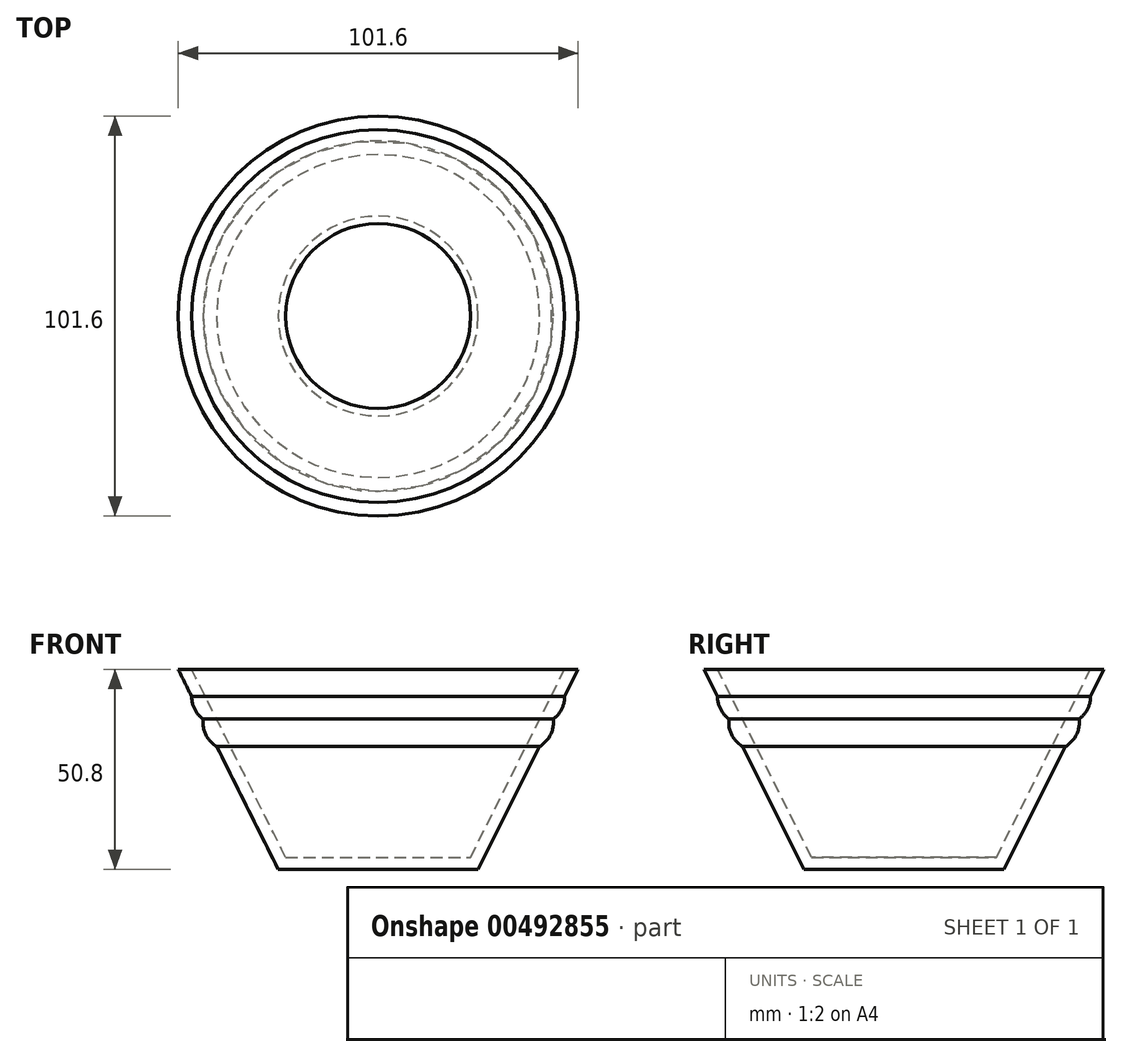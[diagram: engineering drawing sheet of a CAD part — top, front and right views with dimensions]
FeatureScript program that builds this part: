
annotation { "Feature Type Name" : "Feature", "Feature Type Description" : "" }
export const myFeature = defineFeature(function(context is Context, id is Id, definition is map)
    precondition{}
    {
        {
            var Q0;
            Q0=qCreatedBy(makeId("Front.planeOp"),FACE);
            var sketch = newSketch(context, id + "F0", { "sketchPlane" : qUnion([Q0])});
            skLineSegment(sketch, "E0", {"start": v(0, 0) * mm, "end": v(0, 50.8) * mm, "construction": true});
            skLineSegment(sketch, "E1", {"start": v(0, 0) * mm, "end": v(25.4, 0) * mm});
            skLineSegment(sketch, "E2", {"start": v(25.4, 0) * mm, "end": v(50.8, 50.8) * mm});
            skLineSegment(sketch, "E3.0", {"start": v(23.5, 3.07) * mm, "end": v(47.36, 50.8) * mm});
            skLineSegment(sketch, "E3.1", {"start": v(0, 3.07) * mm, "end": v(23.5, 3.07) * mm});
            skLineSegment(sketch, "E4", {"start": v(47.36, 50.8) * mm, "end": v(50.8, 50.8) * mm});
            skLineSegment(sketch, "E5", {"start": v(0, 3.07) * mm, "end": v(0, 0) * mm});
            skArc(sketch, "E6", {"start": v(44.5, 38.2) * mm, "mid": v(46.63, 40.74) * mm, "end": v(47.38, 43.97) * mm});
            skArc(sketch, "E7", {"start": v(41.02, 31.25) * mm, "mid": v(43.79, 34.2) * mm, "end": v(44.5, 38.2) * mm});
            skSolve(sketch);
        }
        {
            var Q0;
            Q0=makeQuery(id+"F0.imprint","IMPRINT",FACE,{"disambiguationData":[TD([[makeQuery(id+"F0.imprint","IMPRINT",EDGE,{"derivedFrom":sQuery(id+"F0.wireOp",EDGE,"E1")}),1.0]])]});
            var Q1;
            {var subQ0=sQuery(id+"F0.wireOp",EDGE,"E6");Q1=makeQuery(id+"F0.imprint","IMPRINT",FACE,{"disambiguationData":[TD([[makeQuery(id+"F0.imprint","IMPRINT",EDGE,{"derivedFrom":subQ0}),1.0]])]});}
            var Q2;
            {var subQ0=sQuery(id+"F0.wireOp",EDGE,"E7");Q2=makeQuery(id+"F0.imprint","IMPRINT",FACE,{"disambiguationData":[TD([[makeQuery(id+"F0.imprint","IMPRINT",EDGE,{"derivedFrom":subQ0}),1.0]])]});}
            var Q3;
            Q3=sQuery(id+"F0.wireOp",EDGE,"E0");
            revolve(context, id + "F1", {"entities" : qUnion([Q0, Q1, Q2]), "axis" : qUnion([Q3]), "revolveType" : RevolveType.FULL});
        }
    });
